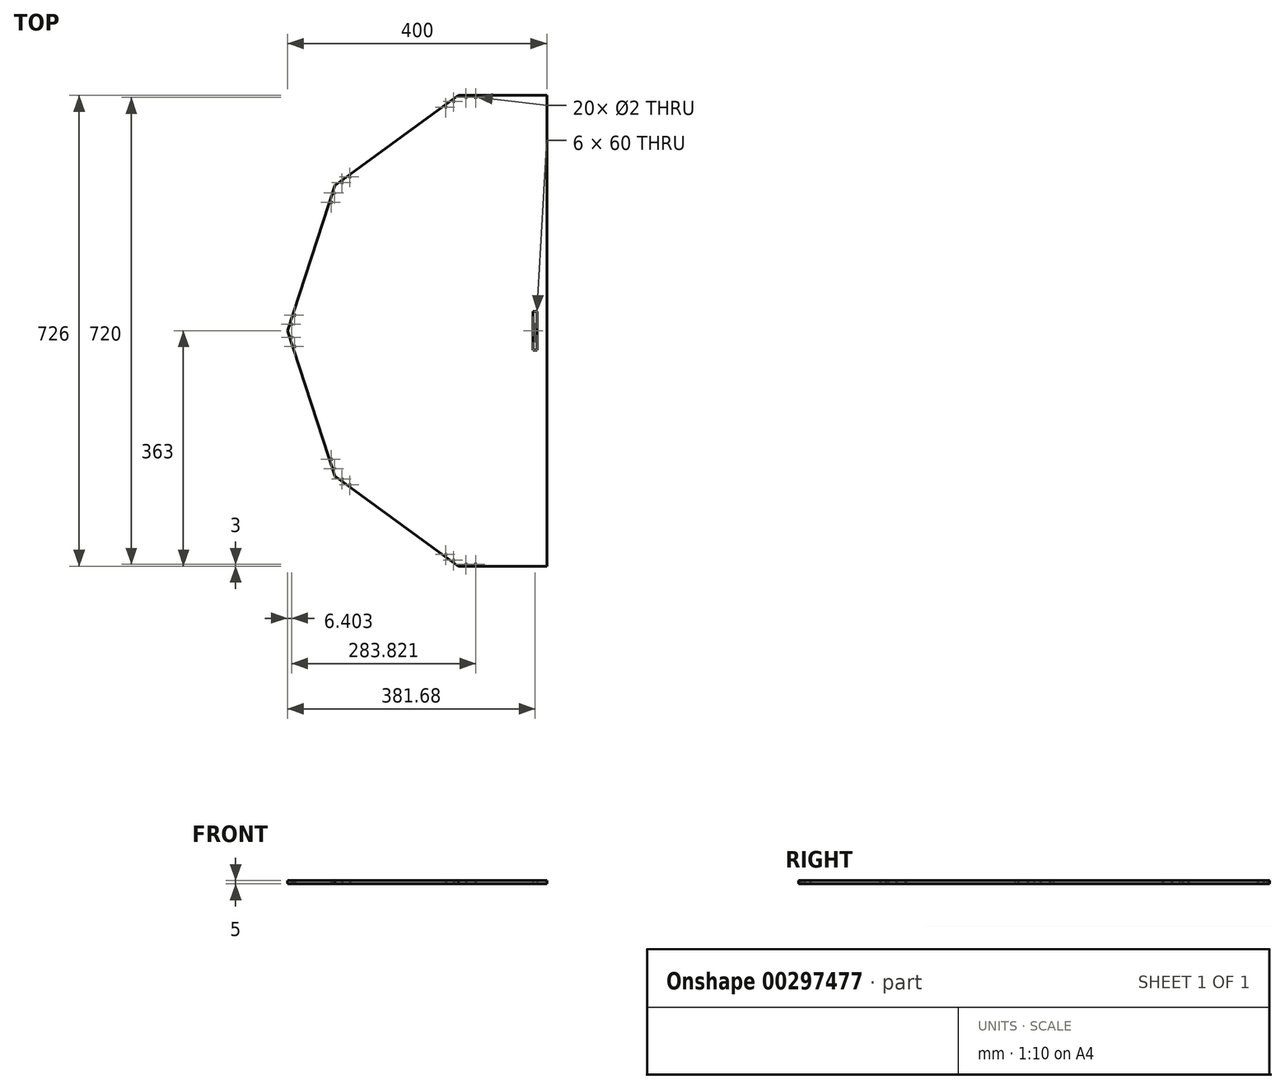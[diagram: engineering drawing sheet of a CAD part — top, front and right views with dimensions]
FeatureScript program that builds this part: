
annotation { "Feature Type Name" : "Feature", "Feature Type Description" : "" }
export const myFeature = defineFeature(function(context is Context, id is Id, definition is map)
    precondition{}
    {
        {
            var Q0;
            Q0=qCreatedBy(makeId("Top.planeOp"),FACE);
            var sketch = newSketch(context, id + "F0", { "sketchPlane" : qUnion([Q0])});
            skLineSegment(sketch, "E0.2", {"start": v(18.32, -363) * mm, "end": v(-117.95, -363) * mm});
            skLineSegment(sketch, "E0.3", {"start": v(-117.95, -363) * mm, "end": v(-308.79, -224.35) * mm});
            skLineSegment(sketch, "E0.4", {"start": v(-308.79, -224.35) * mm, "end": v(-381.68, 0) * mm});
            skLineSegment(sketch, "E0.5", {"start": v(-381.68, 0) * mm, "end": v(-308.79, 224.35) * mm});
            skLineSegment(sketch, "E0.6", {"start": v(-308.79, 224.35) * mm, "end": v(-117.95, 363) * mm});
            skLineSegment(sketch, "E0.7", {"start": v(-117.95, 363) * mm, "end": v(18.32, 363) * mm});
            skCircle(sketch, "E1.3.1", {"center": v(-125.48, 353.82) * mm, "radius": 1 * mm});
            skCircle(sketch, "E1.3.3", {"center": v(-137.61, 345) * mm, "radius": 1 * mm});
            skCircle(sketch, "E1.4.1", {"center": v(-309.48, 212.5) * mm, "radius": 1 * mm});
            skCircle(sketch, "E1.4.3", {"center": v(-314.12, 198.23) * mm, "radius": 1 * mm});
            skCircle(sketch, "E1.5.1", {"center": v(-375.28, -10) * mm, "radius": 1 * mm});
            skCircle(sketch, "E1.5.3", {"center": v(-370.64, -24.27) * mm, "radius": 1 * mm});
            skCircle(sketch, "E1.6.1", {"center": v(-297.73, -228.67) * mm, "radius": 1 * mm});
            skCircle(sketch, "E1.6.3", {"center": v(-285.6, -237.49) * mm, "radius": 1 * mm});
            skCircle(sketch, "E1.7.1", {"center": v(-106.46, -360) * mm, "radius": 1 * mm});
            skCircle(sketch, "E1.7.3", {"center": v(-91.46, -360) * mm, "radius": 1 * mm});
            skLineSegment(sketch, "E2.trimOffspring", {"start": v(18.32, 363) * mm, "end": v(18.32, -363) * mm});
            skLineSegment(sketch, "E3.bottom", {"start": v(3, -30) * mm, "end": v(-3, -30) * mm});
            skLineSegment(sketch, "E3.top", {"start": v(3, 30) * mm, "end": v(-3, 30) * mm});
            skLineSegment(sketch, "E3.left", {"start": v(3, -30) * mm, "end": v(3, 30) * mm});
            skLineSegment(sketch, "E3.right", {"start": v(-3, -30) * mm, "end": v(-3, 30) * mm});
            skPoint(sketch, "E3.middle", {"position": v(0, 0) * mm});
            skCircle(sketch, "E4", {"center": v(-106.46, 360) * mm, "radius": 1 * mm});
            skCircle(sketch, "E5", {"center": v(-91.46, 360) * mm, "radius": 1 * mm});
            skCircle(sketch, "E6", {"center": v(-297.73, 228.67) * mm, "radius": 1 * mm});
            skCircle(sketch, "E7", {"center": v(-285.6, 237.49) * mm, "radius": 1 * mm});
            skCircle(sketch, "E8", {"center": v(-375.28, 10) * mm, "radius": 1 * mm});
            skCircle(sketch, "E9", {"center": v(-370.64, 24.27) * mm, "radius": 1 * mm});
            skCircle(sketch, "E10", {"center": v(-314.12, -198.23) * mm, "radius": 1 * mm});
            skCircle(sketch, "E11", {"center": v(-309.48, -212.5) * mm, "radius": 1 * mm});
            skCircle(sketch, "E12", {"center": v(-125.48, -353.82) * mm, "radius": 1 * mm});
            skCircle(sketch, "E13", {"center": v(-137.61, -345) * mm, "radius": 1 * mm});
            skLineSegment(sketch, "E14.bottom", {"start": v(67, 323.3) * mm, "end": v(149.5, 323.3) * mm});
            skCircle(sketch, "E15", {"center": v(217, 173.3) * mm, "radius": 13 * mm});
            skCircle(sketch, "E16.1.0", {"center": v(77.35, 288.2) * mm, "radius": 1.4 * mm});
            skCircle(sketch, "E16.1.1", {"center": v(102.1, 312.96) * mm, "radius": 1.4 * mm});
            skCircle(sketch, "E16.3.0", {"center": v(102.1, 33.65) * mm, "radius": 1.4 * mm});
            skCircle(sketch, "E16.3.1", {"center": v(77.35, 58.4) * mm, "radius": 1.4 * mm});
            skCircle(sketch, "E16.5.0", {"center": v(356.65, 58.4) * mm, "radius": 1.4 * mm});
            skCircle(sketch, "E16.5.1", {"center": v(331.9, 33.65) * mm, "radius": 1.4 * mm});
            skCircle(sketch, "E16.7.0", {"center": v(331.9, 312.96) * mm, "radius": 1.4 * mm});
            skCircle(sketch, "E16.7.1", {"center": v(356.65, 288.2) * mm, "radius": 1.4 * mm});
            skArc(sketch, "E17", {"start": v(77, -219.2) * mm, "mid": v(79.5, -216.7) * mm, "end": v(77, -214.2) * mm});
            skArc(sketch, "E18", {"start": v(149.5, 313.3) * mm, "mid": v(152, 310.8) * mm, "end": v(154.5, 313.3) * mm});
            skCircle(sketch, "E19", {"center": v(217, 151.3) * mm, "radius": 1.4 * mm});
            skCircle(sketch, "E20", {"center": v(111, -294.7) * mm, "radius": 1.4 * mm});
            skCircle(sketch, "E21", {"center": v(136, -294.7) * mm, "radius": 1.4 * mm});
            skLineSegment(sketch, "E22", {"start": v(67, 323.3) * mm, "end": v(67, -214.2) * mm});
            skLineSegment(sketch, "E23", {"start": v(367, -301.7) * mm, "end": v(367, -219.2) * mm});
            skLineSegment(sketch, "E24", {"start": v(77, -219.2) * mm, "end": v(67, -219.2) * mm});
            skLineSegment(sketch, "E25", {"start": v(77, -214.2) * mm, "end": v(67, -214.2) * mm});
            skLineSegment(sketch, "E26", {"start": v(149.5, 313.3) * mm, "end": v(149.5, 323.3) * mm});
            skLineSegment(sketch, "E27", {"start": v(154.5, 313.3) * mm, "end": v(154.5, 323.3) * mm});
            skLineSegment(sketch, "E28.trimOffspring", {"start": v(67, -219.2) * mm, "end": v(67, -301.7) * mm});
            skLineSegment(sketch, "E29.trimOffspring", {"start": v(154.5, 323.3) * mm, "end": v(279.5, 323.3) * mm});
            skLineSegment(sketch, "E30.MirrorCS", {"start": v(357, -219.2) * mm, "end": v(367, -219.2) * mm});
            skLineSegment(sketch, "E31.MirrorCS", {"start": v(357, -214.2) * mm, "end": v(367, -214.2) * mm});
            skLineSegment(sketch, "E32.MirrorCS", {"start": v(284.5, 313.3) * mm, "end": v(284.5, 323.3) * mm});
            skLineSegment(sketch, "E33.MirrorCS", {"start": v(279.5, 313.3) * mm, "end": v(279.5, 323.3) * mm});
            skLineSegment(sketch, "E34.trimOffspring", {"start": v(284.5, 323.3) * mm, "end": v(367, 323.3) * mm});
            skLineSegment(sketch, "E35.trimOffspring", {"start": v(367, -214.2) * mm, "end": v(367, 323.3) * mm});
            skCircle(sketch, "E36.MirrorC", {"center": v(217, 195.3) * mm, "radius": 1.4 * mm});
            skArc(sketch, "E37.MirrorCS", {"start": v(357, -219.2) * mm, "mid": v(354.5, -216.7) * mm, "end": v(357, -214.2) * mm});
            skArc(sketch, "E38.MirrorCS", {"start": v(284.5, 313.3) * mm, "mid": v(282, 310.8) * mm, "end": v(279.5, 313.3) * mm});
            skCircle(sketch, "E39.MirrorC", {"center": v(298, -294.7) * mm, "radius": 1.4 * mm});
            skCircle(sketch, "E40.MirrorC", {"center": v(323, -294.7) * mm, "radius": 1.4 * mm});
            skLineSegment(sketch, "E41", {"start": v(67, -301.7) * mm, "end": v(367, -301.7) * mm});
            skSolve(sketch);
        }
        {
            var Q0;
            Q0=makeQuery(id+"F0.imprint","IMPRINT",FACE,{"disambiguationData":[TD([[makeQuery(id+"F0.imprint","IMPRINT",EDGE,{"derivedFrom":sQuery(id+"F0.wireOp",EDGE,"E0.2")}),-1.0]])]});
            extrude(context, id + "F1", {"entities" : qUnion([Q0]), "depth" : 5 * mm});
        }
    });
